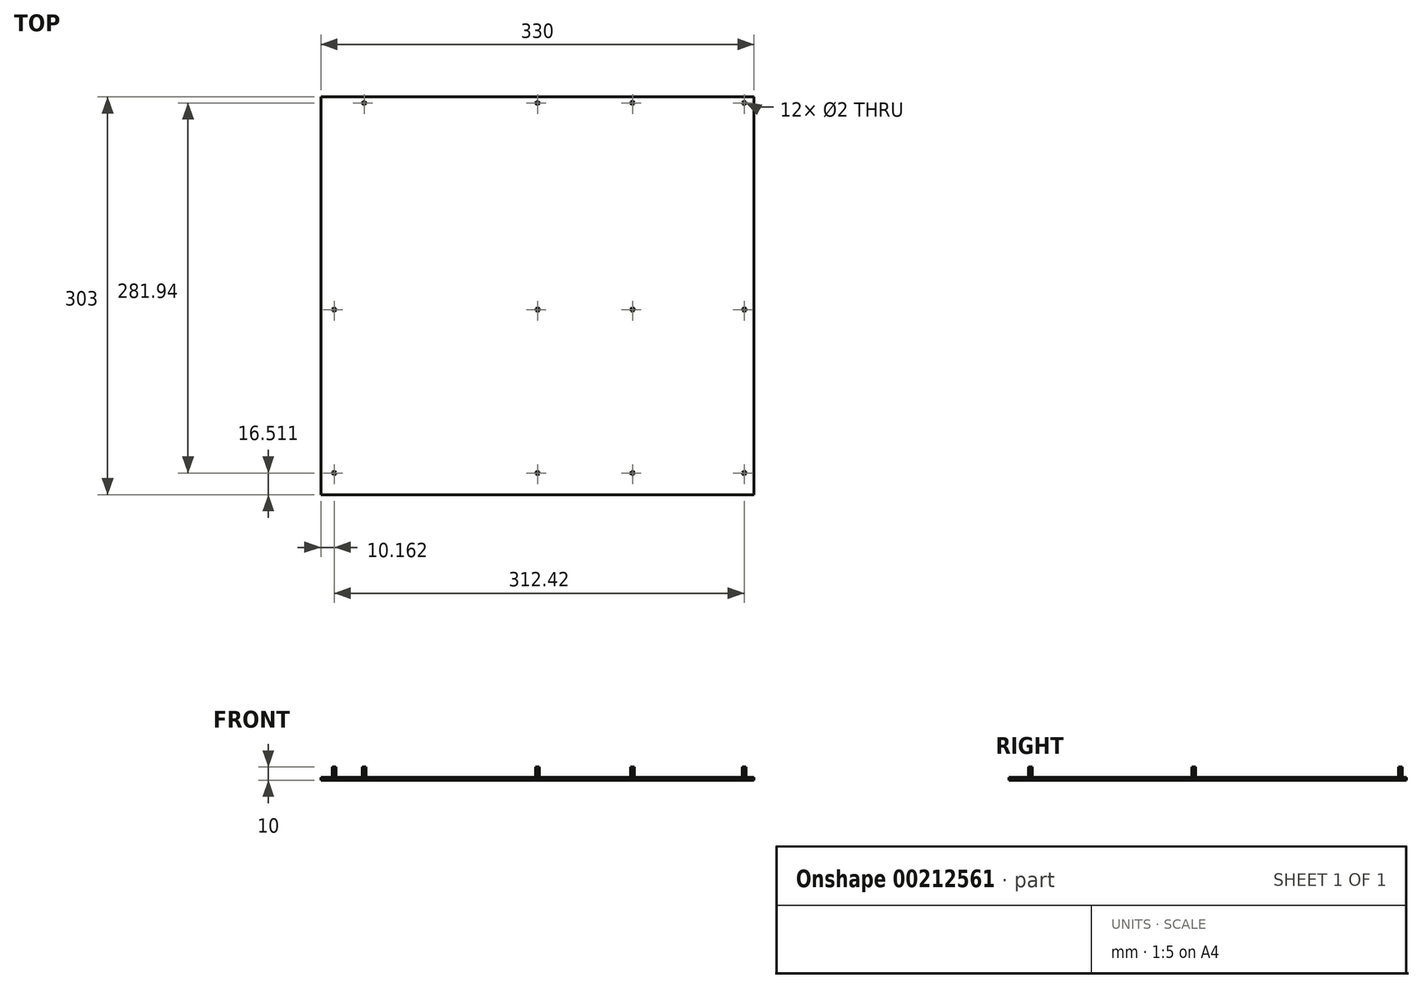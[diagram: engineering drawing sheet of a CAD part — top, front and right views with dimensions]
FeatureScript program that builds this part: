
annotation { "Feature Type Name" : "Feature", "Feature Type Description" : "" }
export const myFeature = defineFeature(function(context is Context, id is Id, definition is map)
    precondition{}
    {
        {
            var Q0;
            Q0=qCreatedBy(makeId("Top.planeOp"),FACE);
            var sketch = newSketch(context, id + "F0", { "sketchPlane" : qUnion([Q0])});
            skLineSegment(sketch, "E0.bottom", {"start": v(-183.37, 154.16) * mm, "end": v(146.63, 154.16) * mm});
            skLineSegment(sketch, "E0.top", {"start": v(-183.37, -148.84) * mm, "end": v(146.63, -148.84) * mm});
            skLineSegment(sketch, "E0.left", {"start": v(-183.37, 154.16) * mm, "end": v(-183.37, -148.84) * mm});
            skLineSegment(sketch, "E0.right", {"start": v(146.63, 154.16) * mm, "end": v(146.63, -148.84) * mm});
            skSolve(sketch);
        }
        {
            var Q0;
            Q0=makeQuery(id+"F0.imprint","IMPRINT",FACE,{"disambiguationData":[TD([[makeQuery(id+"F0.imprint","IMPRINT",EDGE,{"derivedFrom":sQuery(id+"F0.wireOp",EDGE,"E0.bottom")}),-1.0]])]});
            extrude(context, id + "F1", {"entities" : qUnion([Q0]), "depth" : 2 * mm});
        }
        {
            var Q0;
            Q0=makeQuery(id+"F1.opExtrude","CAP_FACE",FACE,{"disambiguationData":[OSD([sQuery(id+"F0.wireOp",EDGE,"E0.bottom"),sQuery(id+"F0.wireOp",EDGE,"E0.top"),sQuery(id+"F0.wireOp",EDGE,"E0.left"),sQuery(id+"F0.wireOp",EDGE,"E0.right")])],"isStart":false});
            var sketch = newSketch(context, id + "F2", { "sketchPlane" : qUnion([Q0])});
            skCircle(sketch, "E1", {"center": v(-173.2, -132.33) * mm, "radius": 2.06 * mm});
            skCircle(sketch, "E2", {"center": v(-173.2, -7.87) * mm, "radius": 2.06 * mm});
            skCircle(sketch, "E3", {"center": v(-150.35, 149.61) * mm, "radius": 2.06 * mm});
            skCircle(sketch, "E4", {"center": v(-18.27, -132.33) * mm, "radius": 2.06 * mm});
            skCircle(sketch, "E5", {"center": v(-18.27, -7.87) * mm, "radius": 2.06 * mm});
            skCircle(sketch, "E6", {"center": v(-18.27, 149.61) * mm, "radius": 2.06 * mm});
            skCircle(sketch, "E7", {"center": v(54.12, 149.61) * mm, "radius": 2.06 * mm});
            skCircle(sketch, "E8", {"center": v(54.12, -7.87) * mm, "radius": 2.06 * mm});
            skCircle(sketch, "E9", {"center": v(54.12, -132.33) * mm, "radius": 2.06 * mm});
            skCircle(sketch, "E10", {"center": v(139.21, 149.61) * mm, "radius": 2.06 * mm});
            skCircle(sketch, "E11", {"center": v(139.21, -7.87) * mm, "radius": 2.06 * mm});
            skCircle(sketch, "E12", {"center": v(139.21, -132.33) * mm, "radius": 2.06 * mm});
            skSolve(sketch);
        }
        {
            var Q0;
            Q0=sQuery(id+"F2.wireOp",VERTEX,"E3.center");
            var Q1;
            Q1=sQuery(id+"F2.wireOp",VERTEX,"E2.center");
            var Q2;
            Q2=sQuery(id+"F2.wireOp",VERTEX,"E4.center");
            var Q3;
            Q3=sQuery(id+"F2.wireOp",VERTEX,"E1.center");
            var Q4;
            Q4=sQuery(id+"F2.wireOp",VERTEX,"E5.center");
            var Q5;
            Q5=sQuery(id+"F2.wireOp",VERTEX,"E6.center");
            var Q6;
            Q6=sQuery(id+"F2.wireOp",VERTEX,"E12.center");
            var Q7;
            Q7=sQuery(id+"F2.wireOp",VERTEX,"E7.center");
            var Q8;
            Q8=sQuery(id+"F2.wireOp",VERTEX,"E11.center");
            var Q9;
            Q9=sQuery(id+"F2.wireOp",VERTEX,"E10.center");
            var Q10;
            Q10=sQuery(id+"F2.wireOp",VERTEX,"E9.center");
            var Q11;
            Q11=sQuery(id+"F2.wireOp",VERTEX,"E8.center");
            var Q12;
            Q12=makeQuery(id+"F1.opExtrude","SWEPT_BODY",BODY,{"disambiguationData":[OSD([sQuery(id+"F0.wireOp",EDGE,"E0.bottom"),sQuery(id+"F0.wireOp",EDGE,"E0.top"),sQuery(id+"F0.wireOp",EDGE,"E0.left"),sQuery(id+"F0.wireOp",EDGE,"E0.right")])]});
            hole(context, id + "F3", {"style" : HoleStyle.SIMPLE, "endStyle" : HoleEndStyle.THROUGH, "holeDiameter" : 2 * mm, "locations" : qUnion([Q0, Q1, Q2, Q3, Q4, Q5, Q6, Q7, Q8, Q9, Q10, Q11]), "scope" : qUnion([Q12]), "tappedDepth" : 12 * mm, "tapClearance" : 3});
        }
        {
            var Q0;
            Q0=makeQuery(id+"F1.opExtrude","CAP_FACE",FACE,{"disambiguationData":[OSD([sQuery(id+"F0.wireOp",EDGE,"E0.bottom"),sQuery(id+"F0.wireOp",EDGE,"E0.top"),sQuery(id+"F0.wireOp",EDGE,"E0.left"),sQuery(id+"F0.wireOp",EDGE,"E0.right")])],"isStart":false});
            var sketch = newSketch(context, id + "F4", { "sketchPlane" : qUnion([Q0])});
            skCircle(sketch, "E13.cCircle", {"center": v(-173.2, -132.33) * mm, "radius": 1.25 * mm, "construction": true});
            skLineSegment(sketch, "E13.0", {"start": v(-174.28, -131.37) * mm, "end": v(-172.91, -130.92) * mm});
            skLineSegment(sketch, "E13.1", {"start": v(-172.91, -130.92) * mm, "end": v(-171.84, -131.88) * mm});
            skLineSegment(sketch, "E13.2", {"start": v(-171.84, -131.88) * mm, "end": v(-172.13, -133.3) * mm});
            skLineSegment(sketch, "E13.3", {"start": v(-172.13, -133.3) * mm, "end": v(-173.5, -133.74) * mm});
            skLineSegment(sketch, "E13.4", {"start": v(-173.5, -133.74) * mm, "end": v(-174.58, -132.78) * mm});
            skLineSegment(sketch, "E13.5", {"start": v(-174.58, -132.78) * mm, "end": v(-174.28, -131.37) * mm});
            skPoint(sketch, "E13.0.midPoint", {"position": v(-173.6, -131.14) * mm});
            skCircle(sketch, "E14.cCircle", {"center": v(-173.2, -7.87) * mm, "radius": 1.25 * mm, "construction": true});
            skLineSegment(sketch, "E14.0", {"start": v(-173.44, -6.45) * mm, "end": v(-172.1, -6.95) * mm});
            skLineSegment(sketch, "E14.1", {"start": v(-172.1, -6.95) * mm, "end": v(-171.86, -8.38) * mm});
            skLineSegment(sketch, "E14.2", {"start": v(-171.86, -8.38) * mm, "end": v(-172.97, -9.3) * mm});
            skLineSegment(sketch, "E14.3", {"start": v(-172.97, -9.3) * mm, "end": v(-174.32, -8.78) * mm});
            skLineSegment(sketch, "E14.4", {"start": v(-174.32, -8.78) * mm, "end": v(-174.56, -7.36) * mm});
            skLineSegment(sketch, "E14.5", {"start": v(-174.56, -7.36) * mm, "end": v(-173.44, -6.45) * mm});
            skPoint(sketch, "E14.0.midPoint", {"position": v(-172.77, -6.7) * mm});
            skCircle(sketch, "E15.cCircle", {"center": v(-150.35, 149.61) * mm, "radius": 1.25 * mm, "construction": true});
            skLineSegment(sketch, "E15.0", {"start": v(-151.07, 150.86) * mm, "end": v(-149.63, 150.86) * mm});
            skLineSegment(sketch, "E15.1", {"start": v(-149.63, 150.86) * mm, "end": v(-148.9, 149.61) * mm});
            skLineSegment(sketch, "E15.2", {"start": v(-148.9, 149.61) * mm, "end": v(-149.63, 148.36) * mm});
            skLineSegment(sketch, "E15.3", {"start": v(-149.63, 148.36) * mm, "end": v(-151.07, 148.36) * mm});
            skLineSegment(sketch, "E15.4", {"start": v(-151.07, 148.36) * mm, "end": v(-151.8, 149.61) * mm});
            skLineSegment(sketch, "E15.5", {"start": v(-151.8, 149.61) * mm, "end": v(-151.07, 150.86) * mm});
            skPoint(sketch, "E15.0.midPoint", {"position": v(-150.35, 150.86) * mm});
            skCircle(sketch, "E16.cCircle", {"center": v(-18.27, 149.61) * mm, "radius": 1.25 * mm, "construction": true});
            skLineSegment(sketch, "E16.0", {"start": v(-18.99, 150.86) * mm, "end": v(-17.55, 150.86) * mm});
            skLineSegment(sketch, "E16.1", {"start": v(-17.55, 150.86) * mm, "end": v(-16.82, 149.61) * mm});
            skLineSegment(sketch, "E16.2", {"start": v(-16.82, 149.61) * mm, "end": v(-17.55, 148.36) * mm});
            skLineSegment(sketch, "E16.3", {"start": v(-17.55, 148.36) * mm, "end": v(-18.99, 148.36) * mm});
            skLineSegment(sketch, "E16.4", {"start": v(-18.99, 148.36) * mm, "end": v(-19.71, 149.61) * mm});
            skLineSegment(sketch, "E16.5", {"start": v(-19.71, 149.61) * mm, "end": v(-18.99, 150.86) * mm});
            skPoint(sketch, "E16.0.midPoint", {"position": v(-18.27, 150.86) * mm});
            skCircle(sketch, "E17.cCircle", {"center": v(54.12, 149.61) * mm, "radius": 1.25 * mm, "construction": true});
            skLineSegment(sketch, "E17.0", {"start": v(55.24, 148.7) * mm, "end": v(53.89, 148.19) * mm});
            skLineSegment(sketch, "E17.1", {"start": v(53.89, 148.19) * mm, "end": v(52.77, 149.1) * mm});
            skLineSegment(sketch, "E17.2", {"start": v(52.77, 149.1) * mm, "end": v(53, 150.53) * mm});
            skLineSegment(sketch, "E17.3", {"start": v(53, 150.53) * mm, "end": v(54.36, 151.03) * mm});
            skLineSegment(sketch, "E17.4", {"start": v(54.36, 151.03) * mm, "end": v(55.47, 150.12) * mm});
            skLineSegment(sketch, "E17.5", {"start": v(55.47, 150.12) * mm, "end": v(55.24, 148.7) * mm});
            skPoint(sketch, "E17.0.midPoint", {"position": v(54.56, 148.44) * mm});
            skCircle(sketch, "E18.cCircle", {"center": v(139.21, 149.61) * mm, "radius": 1.25 * mm, "construction": true});
            skLineSegment(sketch, "E18.0", {"start": v(139.45, 148.19) * mm, "end": v(138.1, 148.7) * mm});
            skLineSegment(sketch, "E18.1", {"start": v(138.1, 148.7) * mm, "end": v(137.86, 150.12) * mm});
            skLineSegment(sketch, "E18.2", {"start": v(137.86, 150.12) * mm, "end": v(138.98, 151.03) * mm});
            skLineSegment(sketch, "E18.3", {"start": v(138.98, 151.03) * mm, "end": v(140.33, 150.53) * mm});
            skLineSegment(sketch, "E18.4", {"start": v(140.33, 150.53) * mm, "end": v(140.56, 149.1) * mm});
            skLineSegment(sketch, "E18.5", {"start": v(140.56, 149.1) * mm, "end": v(139.45, 148.19) * mm});
            skPoint(sketch, "E18.0.midPoint", {"position": v(138.77, 148.44) * mm});
            skCircle(sketch, "E19.cCircle", {"center": v(139.21, -7.87) * mm, "radius": 1.25 * mm, "construction": true});
            skLineSegment(sketch, "E19.0", {"start": v(137.96, -8.6) * mm, "end": v(137.96, -7.15) * mm});
            skLineSegment(sketch, "E19.1", {"start": v(137.96, -7.15) * mm, "end": v(139.21, -6.43) * mm});
            skLineSegment(sketch, "E19.2", {"start": v(139.21, -6.43) * mm, "end": v(140.46, -7.15) * mm});
            skLineSegment(sketch, "E19.3", {"start": v(140.46, -7.15) * mm, "end": v(140.46, -8.6) * mm});
            skLineSegment(sketch, "E19.4", {"start": v(140.46, -8.6) * mm, "end": v(139.21, -9.31) * mm});
            skLineSegment(sketch, "E19.5", {"start": v(139.21, -9.31) * mm, "end": v(137.96, -8.6) * mm});
            skPoint(sketch, "E19.0.midPoint", {"position": v(137.96, -7.87) * mm});
            skCircle(sketch, "E20.cCircle", {"center": v(54.12, -7.87) * mm, "radius": 1.25 * mm, "construction": true});
            skLineSegment(sketch, "E20.0", {"start": v(52.7, -7.61) * mm, "end": v(53.64, -6.51) * mm});
            skLineSegment(sketch, "E20.1", {"start": v(53.64, -6.51) * mm, "end": v(55.06, -6.77) * mm});
            skLineSegment(sketch, "E20.2", {"start": v(55.06, -6.77) * mm, "end": v(55.54, -8.13) * mm});
            skLineSegment(sketch, "E20.3", {"start": v(55.54, -8.13) * mm, "end": v(54.6, -9.23) * mm});
            skLineSegment(sketch, "E20.4", {"start": v(54.6, -9.23) * mm, "end": v(53.19, -8.97) * mm});
            skLineSegment(sketch, "E20.5", {"start": v(53.19, -8.97) * mm, "end": v(52.7, -7.61) * mm});
            skPoint(sketch, "E20.0.midPoint", {"position": v(53.17, -7.06) * mm});
            skCircle(sketch, "E21.cCircle", {"center": v(-18.27, -7.87) * mm, "radius": 1.25 * mm, "construction": true});
            skLineSegment(sketch, "E21.0", {"start": v(-17.02, -7.15) * mm, "end": v(-17.02, -8.6) * mm});
            skLineSegment(sketch, "E21.1", {"start": v(-17.02, -8.6) * mm, "end": v(-18.27, -9.31) * mm});
            skLineSegment(sketch, "E21.2", {"start": v(-18.27, -9.31) * mm, "end": v(-19.52, -8.6) * mm});
            skLineSegment(sketch, "E21.3", {"start": v(-19.52, -8.6) * mm, "end": v(-19.52, -7.15) * mm});
            skLineSegment(sketch, "E21.4", {"start": v(-19.52, -7.15) * mm, "end": v(-18.27, -6.43) * mm});
            skLineSegment(sketch, "E21.5", {"start": v(-18.27, -6.43) * mm, "end": v(-17.02, -7.15) * mm});
            skPoint(sketch, "E21.0.midPoint", {"position": v(-17.02, -7.87) * mm});
            skCircle(sketch, "E22.cCircle", {"center": v(-18.27, -132.33) * mm, "radius": 1.25 * mm, "construction": true});
            skLineSegment(sketch, "E22.0", {"start": v(-18.33, -130.89) * mm, "end": v(-17.05, -131.56) * mm});
            skLineSegment(sketch, "E22.1", {"start": v(-17.05, -131.56) * mm, "end": v(-16.99, -133) * mm});
            skLineSegment(sketch, "E22.2", {"start": v(-16.99, -133) * mm, "end": v(-18.2, -133.77) * mm});
            skLineSegment(sketch, "E22.3", {"start": v(-18.2, -133.77) * mm, "end": v(-19.49, -133.1) * mm});
            skLineSegment(sketch, "E22.4", {"start": v(-19.49, -133.1) * mm, "end": v(-19.55, -131.66) * mm});
            skLineSegment(sketch, "E22.5", {"start": v(-19.55, -131.66) * mm, "end": v(-18.33, -130.89) * mm});
            skPoint(sketch, "E22.0.midPoint", {"position": v(-17.69, -131.22) * mm});
            skCircle(sketch, "E23.cCircle", {"center": v(54.12, -132.33) * mm, "radius": 1.25 * mm, "construction": true});
            skLineSegment(sketch, "E23.0", {"start": v(52.68, -132.39) * mm, "end": v(53.35, -131.11) * mm});
            skLineSegment(sketch, "E23.1", {"start": v(53.35, -131.11) * mm, "end": v(54.8, -131.05) * mm});
            skLineSegment(sketch, "E23.2", {"start": v(54.8, -131.05) * mm, "end": v(55.56, -132.27) * mm});
            skLineSegment(sketch, "E23.3", {"start": v(55.56, -132.27) * mm, "end": v(54.9, -133.55) * mm});
            skLineSegment(sketch, "E23.4", {"start": v(54.9, -133.55) * mm, "end": v(53.45, -133.6) * mm});
            skLineSegment(sketch, "E23.5", {"start": v(53.45, -133.6) * mm, "end": v(52.68, -132.39) * mm});
            skPoint(sketch, "E23.0.midPoint", {"position": v(53.01, -131.75) * mm});
            skCircle(sketch, "E24.cCircle", {"center": v(139.21, -132.33) * mm, "radius": 1.25 * mm, "construction": true});
            skLineSegment(sketch, "E24.0", {"start": v(138.9, -130.92) * mm, "end": v(140.28, -131.35) * mm});
            skLineSegment(sketch, "E24.1", {"start": v(140.28, -131.35) * mm, "end": v(140.59, -132.76) * mm});
            skLineSegment(sketch, "E24.2", {"start": v(140.59, -132.76) * mm, "end": v(139.52, -133.74) * mm});
            skLineSegment(sketch, "E24.3", {"start": v(139.52, -133.74) * mm, "end": v(138.15, -133.3) * mm});
            skLineSegment(sketch, "E24.4", {"start": v(138.15, -133.3) * mm, "end": v(137.84, -131.9) * mm});
            skLineSegment(sketch, "E24.5", {"start": v(137.84, -131.9) * mm, "end": v(138.9, -130.92) * mm});
            skPoint(sketch, "E24.0.midPoint", {"position": v(139.59, -131.14) * mm});
            skSolve(sketch);
        }
        {
            var Q0;
            Q0 = qSketchRegion(id + "F4", true);
            extrude(context, id + "F5", {"entities" : qUnion([Q0]), "depth" : 8 * mm});
        }
    });
